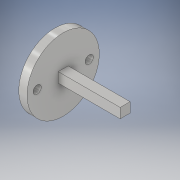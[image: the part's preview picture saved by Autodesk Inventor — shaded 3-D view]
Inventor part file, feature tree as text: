
AUTODESK INVENTOR PART (.ipt)
format: ipt  version: 2019 (Build 230136000, 136)  size: 117,760 bytes
history: native  units: in
note: dims shown in document units (in); Inventor stores cm internally (conversion verified against a paired STEP export)
features: sketch x3, extrude x2, hole x1
ambient origin geometry x8: Origin, YZ Plane, XZ Plane, XY Plane, X Axis, Y Axis, Z Axis, Center Point
bodies: Solid1 (feature_tree)
feature tree (6):
  extrude  "Extrusion1"  Depth=0.1in TaperAngle=0.0deg
  extrude  "Extrusion2"  Depth=0.12in
  hole  "Hole1"  [1 undecoded]
  sketch  "Sketch1"  dims[d0=0.875in d1=0.1in d2=0.0in]
  sketch  "Sketch2"  dims[d3=0.12in d4=0.12in]
  sketch  "Sketch3"  dims[d5=0.06in d6=0.06in d7=0.75in d8=0.0in d9=0.63in d10=0.315in d11=0.098in d12=0.75in d13=0.375in d14=0.25in d15=0.5635in d16=1.0in d17=0.8108in]
note: 1 required parameter value undecoded (feature->parameter linkage not recoverable at this tier; creation-order binding heuristic only, values carry confidence <= 0.55)
